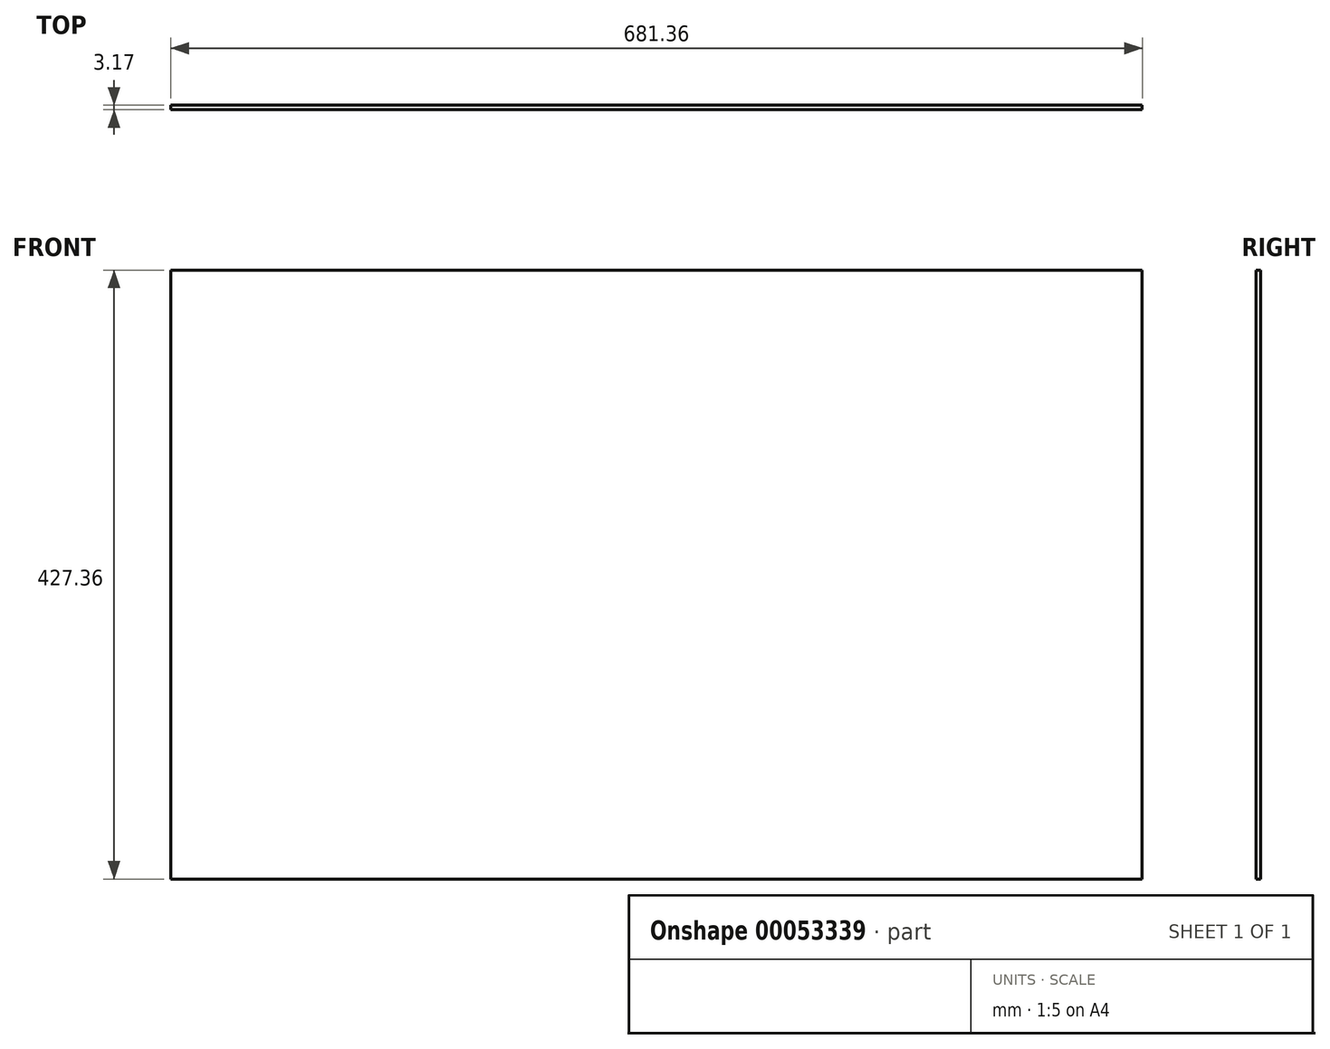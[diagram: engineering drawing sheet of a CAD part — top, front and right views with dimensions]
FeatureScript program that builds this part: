
annotation { "Feature Type Name" : "Feature", "Feature Type Description" : "" }
export const myFeature = defineFeature(function(context is Context, id is Id, definition is map)
    precondition{}
    {
        {
            var Q0;
            Q0=qCreatedBy(makeId("Front.planeOp"),FACE);
            var sketch = newSketch(context, id + "F0", { "sketchPlane" : qUnion([Q0])});
            skLineSegment(sketch, "E0.bottom", {"start": v(-375.88, 253.77) * mm, "end": v(305.48, 253.77) * mm});
            skLineSegment(sketch, "E0.top", {"start": v(-375.88, -173.59) * mm, "end": v(305.48, -173.59) * mm});
            skLineSegment(sketch, "E0.left", {"start": v(-375.88, 253.77) * mm, "end": v(-375.88, -173.59) * mm});
            skLineSegment(sketch, "E0.right", {"start": v(305.48, 253.77) * mm, "end": v(305.48, -173.59) * mm});
            skSolve(sketch);
        }
        {
            var Q0;
            Q0 = qSketchRegion(id + "F0", true);
            extrude(context, id + "F1", {"entities" : qUnion([Q0]), "depth" : 3.17 * mm});
        }
    });
